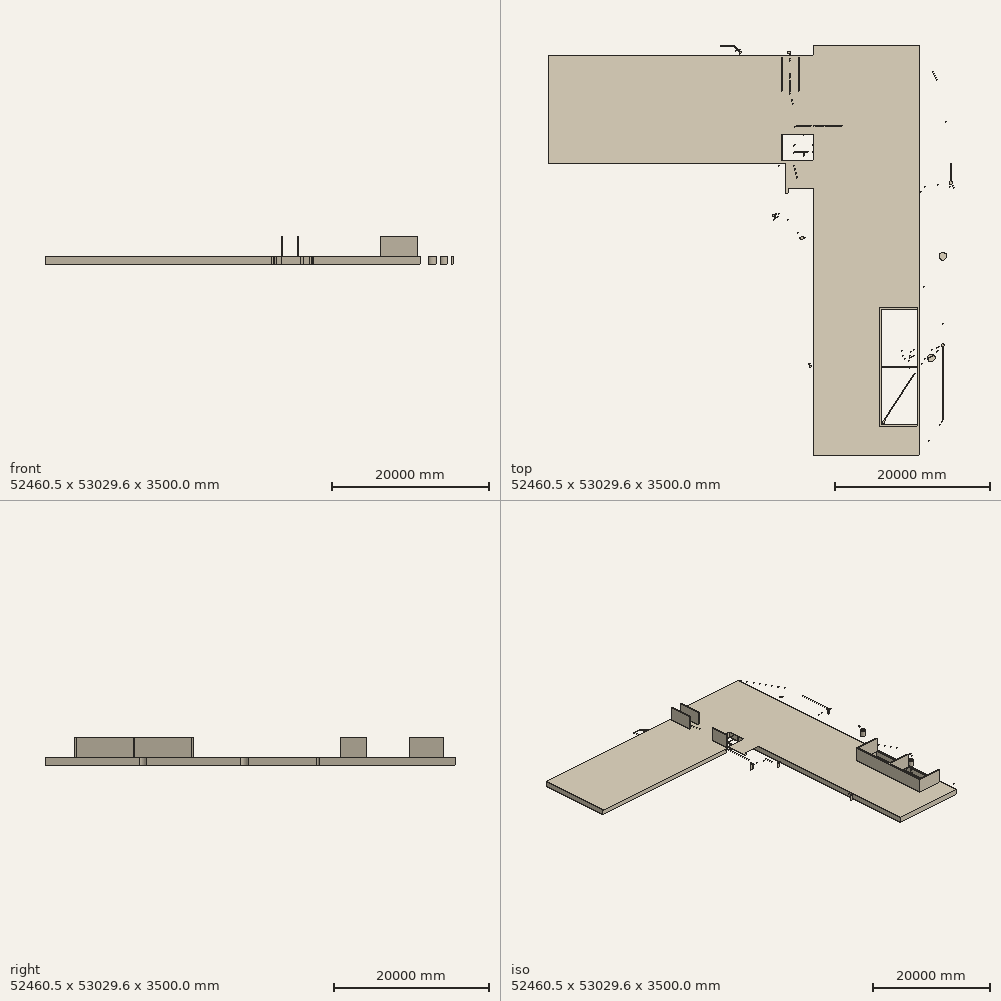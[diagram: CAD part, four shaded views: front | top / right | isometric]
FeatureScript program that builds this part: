
annotation { "Feature Type Name" : "Feature", "Feature Type Description" : "" }
export const myFeature = defineFeature(function(context is Context, id is Id, definition is map)
    precondition{}
    {
        {
            var Q0;
            Q0=qCreatedBy(makeId("Top.planeOp"),FACE);
            var sketch = newSketch(context, id + "F0", { "sketchPlane" : qUnion([Q0])});
            skLineSegment(sketch, "E0", {"start": v(56364.8, 6468.58) * mm, "end": v(56364.8, -31331.42) * mm});
            skLineSegment(sketch, "E1", {"start": v(56364.8, 6468.58) * mm, "end": v(22064.8, 6468.58) * mm});
            skLineSegment(sketch, "E2", {"start": v(56364.8, -31331.42) * mm, "end": v(70064.8, -31331.42) * mm});
            skLineSegment(sketch, "E3", {"start": v(70064.8, -31331.42) * mm, "end": v(70064.8, 21668.58) * mm});
            skLineSegment(sketch, "E4", {"start": v(70064.8, 21668.58) * mm, "end": v(56364.8, 21668.58) * mm});
            skLineSegment(sketch, "E5", {"start": v(22064.8, 20468.58) * mm, "end": v(22064.8, 6468.58) * mm});
            skPoint(sketch, "E6", {"position": v(56364.8, 21668.58) * mm});
            skLineSegment(sketch, "E7", {"start": v(56364.8, 21668.58) * mm, "end": v(56364.8, 20468.58) * mm});
            skLineSegment(sketch, "E8", {"start": v(56364.8, 20468.58) * mm, "end": v(22064.8, 20468.58) * mm});
            skPoint(sketch, "E9", {"position": v(56364.8, 20168.58) * mm});
            skPoint(sketch, "E10", {"position": v(56366.57, 6768.58) * mm});
            skLineSegment(sketch, "E11", {"start": v(56366.57, 6768.58) * mm, "end": v(22064.8, 6768.58) * mm});
            skLineSegment(sketch, "E12", {"start": v(56364.8, 20168.58) * mm, "end": v(22064.8, 20168.58) * mm});
            skLineSegment(sketch, "E13", {"start": v(52221.8, 20168.58) * mm, "end": v(52221.8, 15726.58) * mm});
            skPoint(sketch, "E14", {"position": v(52221.8, 20168.58) * mm});
            skLineSegment(sketch, "E15", {"start": v(52341.8, 20168.58) * mm, "end": v(52341.8, 15726.58) * mm});
            skLineSegment(sketch, "E16", {"start": v(54356.8, 20168.58) * mm, "end": v(54356.8, 15726.58) * mm});
            skLineSegment(sketch, "E17", {"start": v(54476.8, 20168.58) * mm, "end": v(54476.8, 15726.58) * mm});
            skLineSegment(sketch, "E18", {"start": v(56364.8, 6468.58) * mm, "end": v(56364.8, 10201.58) * mm});
            skLineSegment(sketch, "E19", {"start": v(56364.8, 10201.58) * mm, "end": v(52221.8, 10201.58) * mm});
            skLineSegment(sketch, "E20", {"start": v(52221.8, 10201.58) * mm, "end": v(52221.8, 6768.58) * mm});
            skLineSegment(sketch, "E21", {"start": v(52341.8, 10201.58) * mm, "end": v(52341.8, 6768.58) * mm});
            skLineSegment(sketch, "E22", {"start": v(69714.8, -12436.42) * mm, "end": v(65114.8, -12436.42) * mm});
            skLineSegment(sketch, "E23", {"start": v(69714.8, -27316.42) * mm, "end": v(65114.8, -27316.42) * mm});
            skLineSegment(sketch, "E24", {"start": v(69714.8, -31331.42) * mm, "end": v(69714.8, 21668.58) * mm});
            skPoint(sketch, "E25", {"position": v(70064.8, -19876.42) * mm});
            skLineSegment(sketch, "E26", {"start": v(69714.8, -19756.42) * mm, "end": v(65114.8, -19756.42) * mm});
            skLineSegment(sketch, "E27", {"start": v(69714.8, -19996.42) * mm, "end": v(65114.8, -19996.42) * mm});
            skPoint(sketch, "E28.orphan", {"position": v(47856.69, 10201.58) * mm});
            skPoint(sketch, "E29.orphan", {"position": v(52341.8, 11812.01) * mm});
            skLineSegment(sketch, "E30", {"start": v(52221.8, 15726.58) * mm, "end": v(52341.8, 15726.58) * mm});
            skLineSegment(sketch, "E31", {"start": v(54356.8, 15726.58) * mm, "end": v(54476.8, 15726.58) * mm});
            skLineSegment(sketch, "E32", {"start": v(65114.8, -19996.42) * mm, "end": v(65114.8, -19756.42) * mm});
            skLineSegment(sketch, "E33", {"start": v(65114.8, -12436.42) * mm, "end": v(65114.8, -12196.42) * mm});
            skLineSegment(sketch, "E34", {"start": v(65114.8, -12196.42) * mm, "end": v(69714.8, -12196.42) * mm});
            skLineSegment(sketch, "E35", {"start": v(65114.8, -27316.42) * mm, "end": v(65114.8, -27556.42) * mm});
            skLineSegment(sketch, "E36", {"start": v(65114.8, -27556.42) * mm, "end": v(69714.8, -27556.42) * mm});
            skLineSegment(sketch, "E37.bottom", {"start": v(65114.8, -12196.42) * mm, "end": v(64874.8, -12196.42) * mm});
            skLineSegment(sketch, "E37.top", {"start": v(65114.8, -27556.42) * mm, "end": v(64874.8, -27556.42) * mm});
            skLineSegment(sketch, "E37.left", {"start": v(65114.8, -12196.42) * mm, "end": v(65114.8, -27556.42) * mm});
            skLineSegment(sketch, "E37.right", {"start": v(64874.8, -12196.42) * mm, "end": v(64874.8, -27556.42) * mm});
            skLineSegment(sketch, "E38", {"start": v(52664.8, 3178.58) * mm, "end": v(56364.8, 3178.58) * mm});
            skLineSegment(sketch, "E39.trimOffspring", {"start": v(52664.8, 6468.58) * mm, "end": v(52664.8, 3178.58) * mm});
            skLineSegment(sketch, "E40.bottom", {"start": v(52664.8, 3178.58) * mm, "end": v(53121.8, 3178.58) * mm});
            skLineSegment(sketch, "E40.top", {"start": v(52664.8, 2595.58) * mm, "end": v(53121.8, 2595.58) * mm});
            skLineSegment(sketch, "E40.left", {"start": v(52664.8, 3178.58) * mm, "end": v(52664.8, 2595.58) * mm});
            skLineSegment(sketch, "E40.right", {"start": v(53121.8, 3178.58) * mm, "end": v(53121.8, 2595.58) * mm});
            skSolve(sketch);
        }
        {
            var Q0;
            Q0=qCreatedBy(makeId("Top.planeOp"),FACE);
            var sketch = newSketch(context, id + "F1", { "sketchPlane" : qUnion([Q0])});
            skLineSegment(sketch, "E41", {"start": v(53664.8, 6468.58) * mm, "end": v(54182.45, 4536.73) * mm});
            skPoint(sketch, "E42", {"position": v(53664.8, 6468.58) * mm});
            skLineSegment(sketch, "E43", {"start": v(54182.45, 4536.73) * mm, "end": v(54182.45, -2463.27) * mm});
            skLineSegment(sketch, "E44", {"start": v(53828.9, -1109.71) * mm, "end": v(54182.45, -1463.27) * mm});
            skPoint(sketch, "E45", {"position": v(54182.45, -1463.27) * mm});
            skCircle(sketch, "E46", {"center": v(54864.8, -3240.9) * mm, "radius": 212.5 * mm});
            skPoint(sketch, "E47", {"position": v(54857.37, -3028.53) * mm});
            skLineSegment(sketch, "E48", {"start": v(54182.45, -2463.27) * mm, "end": v(54864.44, -3034.46) * mm});
            skPoint(sketch, "E49", {"position": v(70139.8, -8631.42) * mm});
            skPoint(sketch, "E50", {"position": v(73064.8, -26831.42) * mm});
            skLineSegment(sketch, "E51", {"start": v(70139.8, -31081.42) * mm, "end": v(73064.8, -26831.42) * mm});
            skPoint(sketch, "E52", {"position": v(73064.8, -17081.42) * mm});
            skPoint(sketch, "E53", {"position": v(73064.8, -14331.42) * mm});
            skCircle(sketch, "E54", {"center": v(73064.8, -17081.42) * mm, "radius": 212.5 * mm});
            skLineSegment(sketch, "E55", {"start": v(73064.8, -26831.42) * mm, "end": v(73064.8, -17293.92) * mm});
            skLineSegment(sketch, "E56", {"start": v(70139.8, -8631.42) * mm, "end": v(73064.8, -14331.42) * mm});
            skLineSegment(sketch, "E57", {"start": v(73064.8, -14331.42) * mm, "end": v(73064.8, -16868.92) * mm});
            skPoint(sketch, "E58", {"position": v(71564.8, -18731.42) * mm});
            skCircle(sketch, "E59", {"center": v(71564.8, -18731.42) * mm, "radius": 500 * mm});
            skLineSegment(sketch, "E60", {"start": v(72921.87, -17238.65) * mm, "end": v(71901.15, -18361.45) * mm});
            skPoint(sketch, "E61", {"position": v(73064.8, -5581.42) * mm});
            skPoint(sketch, "E62", {"position": v(74064.8, -2831.42) * mm});
            skPoint(sketch, "E63", {"position": v(74064.8, 11668.58) * mm});
            skPoint(sketch, "E64", {"position": v(74064.8, 3918.58) * mm});
            skPoint(sketch, "E65", {"position": v(74064.8, 13768.58) * mm});
            skCircle(sketch, "E66", {"center": v(74064.8, 3918.58) * mm, "radius": 212.5 * mm});
            skLineSegment(sketch, "E67", {"start": v(70139.8, 2668.58) * mm, "end": v(70729.42, 3400.6) * mm});
            skLineSegment(sketch, "E68", {"start": v(70729.42, 3400.6) * mm, "end": v(73854.83, 3885.97) * mm});
            skCircle(sketch, "E69", {"center": v(73064.8, -5581.42) * mm, "radius": 500 * mm});
            skLineSegment(sketch, "E70", {"start": v(73064.8, -5581.42) * mm, "end": v(74064.8, -2831.42) * mm});
            skLineSegment(sketch, "E71", {"start": v(74064.8, 3918.58) * mm, "end": v(74064.8, -2831.42) * mm});
            skLineSegment(sketch, "E72", {"start": v(74064.8, 3918.58) * mm, "end": v(74064.8, 11668.58) * mm});
            skLineSegment(sketch, "E73", {"start": v(74064.8, 11668.58) * mm, "end": v(74064.8, 13768.58) * mm});
            skLineSegment(sketch, "E74", {"start": v(74064.8, 13768.58) * mm, "end": v(70139.8, 21418.58) * mm});
            skLineSegment(sketch, "E75", {"start": v(70139.8, 13768.58) * mm, "end": v(71421.55, 12224.42) * mm});
            skLineSegment(sketch, "E76", {"start": v(71421.55, 12224.42) * mm, "end": v(74064.8, 11668.58) * mm});
            skPoint(sketch, "E77", {"position": v(51114.8, -281.42) * mm});
            skLineSegment(sketch, "E78", {"start": v(51114.8, -281.42) * mm, "end": v(53828.9, -1109.71) * mm});
            skCircle(sketch, "E79", {"center": v(51114.8, -281.42) * mm, "radius": 157.5 * mm});
            skLineSegment(sketch, "E80", {"start": v(51567.38, 60.2) * mm, "end": v(51296.06, -828.82) * mm});
            skLineSegment(sketch, "E81", {"start": v(51296.06, -828.82) * mm, "end": v(51894.17, -35.98) * mm});
            skPoint(sketch, "E82", {"position": v(51597.82, -428.82) * mm});
            skPoint(sketch, "E83", {"position": v(51433.45, -378.66) * mm});
            skPoint(sketch, "E84", {"position": v(51265.45, -327.39) * mm});
            skPoint(sketch, "E85", {"position": v(56214.8, -19831.42) * mm});
            skPoint(sketch, "E86", {"position": v(55964.8, -19831.42) * mm});
            skCircle(sketch, "E87", {"center": v(55964.8, -19831.42) * mm, "radius": 157.5 * mm});
            skLineSegment(sketch, "E88", {"start": v(55439.22, -19965.06) * mm, "end": v(56064.44, -19277.27) * mm});
            skLineSegment(sketch, "E89", {"start": v(56064.44, -19277.27) * mm, "end": v(55184.87, -19738.45) * mm});
            skPoint(sketch, "E90", {"position": v(55635.54, -19502.15) * mm});
            skLineSegment(sketch, "E91", {"start": v(55964.8, -19831.42) * mm, "end": v(55214.8, -19081.42) * mm});
            skPoint(sketch, "E92", {"position": v(55853.44, -19720.05) * mm});
            skPoint(sketch, "E93", {"position": v(55807.3, -19831.42) * mm});
            skLineSegment(sketch, "E94", {"start": v(70139.8, -19831.42) * mm, "end": v(71387.08, -17771.2) * mm});
            skLineSegment(sketch, "E95", {"start": v(71387.08, -17771.2) * mm, "end": v(72868.27, -17162.22) * mm});
            skPoint(sketch, "E96", {"position": v(72868.27, -17162.22) * mm});
            skPoint(sketch, "E97", {"position": v(55753.13, -19619.74) * mm});
            skLineSegment(sketch, "E98", {"start": v(47864.8, 6318.58) * mm, "end": v(51563.3, 6318.58) * mm});
            skLineSegment(sketch, "E99", {"start": v(51563.3, 6318.58) * mm, "end": v(51917.8, 6030.87) * mm});
            skLineSegment(sketch, "E100", {"start": v(51917.8, 6030.87) * mm, "end": v(51917.8, 619.15) * mm});
            skLineSegment(sketch, "E101", {"start": v(51917.8, 619.15) * mm, "end": v(51114.8, -281.42) * mm});
            skPoint(sketch, "E102", {"position": v(51917.8, 2559.53) * mm});
            skLineSegment(sketch, "E103", {"start": v(51917.8, 2559.53) * mm, "end": v(52279.66, 2921.39) * mm});
            skLineSegment(sketch, "E104", {"start": v(52279.66, 2921.39) * mm, "end": v(52811.8, 2921.39) * mm});
            skPoint(sketch, "E105", {"position": v(46851.2, 20733.64) * mm});
            skCircle(sketch, "E106", {"center": v(46851.2, 20733.64) * mm, "radius": 157.5 * mm});
            skLineSegment(sketch, "E107", {"start": v(46325.62, 20600) * mm, "end": v(46950.83, 21287.79) * mm});
            skLineSegment(sketch, "E108", {"start": v(46950.83, 21287.79) * mm, "end": v(46071.27, 20826.6) * mm});
            skPoint(sketch, "E109", {"position": v(46521.94, 21062.9) * mm});
            skLineSegment(sketch, "E110", {"start": v(46851.2, 20733.64) * mm, "end": v(45951.46, 21633.38) * mm});
            skPoint(sketch, "E111", {"position": v(46739.84, 20845) * mm});
            skPoint(sketch, "E112", {"position": v(46693.7, 20733.64) * mm});
            skCircle(sketch, "E113", {"center": v(46664.8, 20543.58) * mm, "radius": 55 * mm});
            skPoint(sketch, "E114", {"position": v(46639.53, 20945.32) * mm});
            skLineSegment(sketch, "E115", {"start": v(44664.8, 19768.58) * mm, "end": v(44664.8, 21465.21) * mm});
            skLineSegment(sketch, "E116", {"start": v(45951.46, 21633.38) * mm, "end": v(44322.18, 21633.38) * mm});
            skLineSegment(sketch, "E117", {"start": v(44664.8, 21465.21) * mm, "end": v(44496.64, 21633.38) * mm});
            skCircle(sketch, "E118", {"center": v(44727.7, 20131.27) * mm, "radius": 25 * mm, "construction": true});
            skLineSegment(sketch, "E119", {"start": v(44727.7, 20131.27) * mm, "end": v(44664.8, 19768.58) * mm});
            skCircle(sketch, "E120", {"center": v(53556.8, 20018.58) * mm, "radius": 55 * mm});
            skCircle(sketch, "E121", {"center": v(54282.28, 18938.58) * mm, "radius": 55 * mm});
            skCircle(sketch, "E122", {"center": v(54282.28, 16918.58) * mm, "radius": 55 * mm});
            skPoint(sketch, "E123", {"position": v(52741.8, 19768.58) * mm});
            skLineSegment(sketch, "E124.bottom", {"start": v(52681.3, 19855.08) * mm, "end": v(52802.3, 19855.08) * mm});
            skLineSegment(sketch, "E124.top", {"start": v(52681.3, 19682.08) * mm, "end": v(52802.3, 19682.08) * mm});
            skLineSegment(sketch, "E124.left", {"start": v(52681.3, 19855.08) * mm, "end": v(52681.3, 19682.08) * mm});
            skLineSegment(sketch, "E124.right", {"start": v(52802.3, 19855.08) * mm, "end": v(52802.3, 19682.08) * mm});
            skLineSegment(sketch, "E125", {"start": v(53195.46, 20793.39) * mm, "end": v(53195.46, 15712.6) * mm});
            skLineSegment(sketch, "E126", {"start": v(53195.46, 15712.6) * mm, "end": v(53664.8, 14001.77) * mm});
            skLineSegment(sketch, "E127", {"start": v(53664.8, 14001.77) * mm, "end": v(53664.8, 6468.58) * mm});
            skLineSegment(sketch, "E128", {"start": v(54282.28, 16918.58) * mm, "end": v(53445.11, 16918.58) * mm});
            skLineSegment(sketch, "E129", {"start": v(53445.11, 16918.58) * mm, "end": v(53195.46, 16668.93) * mm});
            skLineSegment(sketch, "E130", {"start": v(54282.28, 18938.58) * mm, "end": v(53415.44, 18938.58) * mm});
            skLineSegment(sketch, "E131", {"start": v(53415.44, 18938.58) * mm, "end": v(53195.46, 18718.6) * mm});
            skLineSegment(sketch, "E132", {"start": v(53556.8, 20018.58) * mm, "end": v(53302.98, 20018.58) * mm});
            skLineSegment(sketch, "E133", {"start": v(53302.98, 20018.58) * mm, "end": v(53195.46, 19911.06) * mm});
            skCircle(sketch, "E134", {"center": v(53671.8, 6828.9) * mm, "radius": 55 * mm});
            skCircle(sketch, "E135", {"center": v(55041.8, 6828.9) * mm, "radius": 55 * mm});
            skCircle(sketch, "E136", {"center": v(56214.8, 8864.58) * mm, "radius": 55 * mm});
            skCircle(sketch, "E137", {"center": v(56214.8, 7944.58) * mm, "radius": 55 * mm});
            skCircle(sketch, "E138", {"center": v(52396.8, 9538.58) * mm, "radius": 55 * mm});
            skCircle(sketch, "E139", {"center": v(55041.8, 10146.58) * mm, "radius": 55 * mm});
            skLineSegment(sketch, "E140", {"start": v(56214.8, 7944.58) * mm, "end": v(53914.8, 7944.58) * mm});
            skLineSegment(sketch, "E141", {"start": v(53914.8, 7944.58) * mm, "end": v(53914.8, 7944.58) * mm});
            skLineSegment(sketch, "E142", {"start": v(53914.8, 7944.58) * mm, "end": v(53664.8, 7694.58) * mm});
            skLineSegment(sketch, "E143", {"start": v(56214.8, 8864.58) * mm, "end": v(53914.8, 8864.58) * mm});
            skLineSegment(sketch, "E144", {"start": v(53914.8, 8864.58) * mm, "end": v(53664.8, 8614.58) * mm});
            skLineSegment(sketch, "E145", {"start": v(55041.8, 10146.58) * mm, "end": v(55041.8, 8979.55) * mm});
            skLineSegment(sketch, "E146", {"start": v(55041.8, 8979.55) * mm, "end": v(54926.84, 8864.58) * mm});
            skLineSegment(sketch, "E147", {"start": v(55041.8, 6828.9) * mm, "end": v(55041.8, 7817.77) * mm});
            skLineSegment(sketch, "E148", {"start": v(55041.8, 7817.77) * mm, "end": v(54915, 7944.58) * mm});
            skLineSegment(sketch, "E149", {"start": v(52396.8, 9538.58) * mm, "end": v(53591.64, 9538.58) * mm});
            skLineSegment(sketch, "E150", {"start": v(53591.64, 9538.58) * mm, "end": v(53664.8, 9465.4) * mm});
            skCircle(sketch, "E151", {"center": v(60014.8, 11278.58) * mm, "radius": 55 * mm});
            skLineSegment(sketch, "E152", {"start": v(60014.8, 11278.58) * mm, "end": v(54006.65, 11278.58) * mm});
            skLineSegment(sketch, "E153", {"start": v(54006.65, 11278.58) * mm, "end": v(53664.8, 10936.75) * mm});
            skCircle(sketch, "E154", {"center": v(53195.46, 20793.39) * mm, "radius": 200 * mm});
            skCircle(sketch, "E155", {"center": v(67706.8, -18221.42) * mm, "radius": 55 * mm});
            skCircle(sketch, "E156", {"center": v(67706.8, -17821.42) * mm, "radius": 55 * mm});
            skCircle(sketch, "E157", {"center": v(68354.8, -18121.42) * mm, "radius": 25 * mm});
            skCircle(sketch, "E158", {"center": v(68354.8, -17921.42) * mm, "radius": 25 * mm});
            skCircle(sketch, "E159", {"center": v(69314.8, -18471.42) * mm, "radius": 55 * mm});
            skCircle(sketch, "E160", {"center": v(69314.8, -17671.42) * mm, "radius": 55 * mm});
            skLineSegment(sketch, "E161", {"start": v(69214.8, -20746.42) * mm, "end": v(69714.8, -20746.42) * mm});
            skLineSegment(sketch, "E162", {"start": v(69214.8, -20746.42) * mm, "end": v(68030.87, -18628.96) * mm});
            skLineSegment(sketch, "E163", {"start": v(68030.87, -18628.96) * mm, "end": v(68030.87, -12507) * mm});
            skLineSegment(sketch, "E164", {"start": v(67706.8, -18221.42) * mm, "end": v(68030.87, -18628.96) * mm});
            skLineSegment(sketch, "E165", {"start": v(68354.8, -18121.42) * mm, "end": v(68445.6, -18254.83) * mm});
            skLineSegment(sketch, "E166", {"start": v(68445.6, -18254.83) * mm, "end": v(68445.6, -19370.69) * mm});
            skLineSegment(sketch, "E167", {"start": v(68445.6, -18254.83) * mm, "end": v(68445.6, -18012.45) * mm});
            skLineSegment(sketch, "E168", {"start": v(68354.8, -17921.42) * mm, "end": v(68445.6, -18012.45) * mm});
            skLineSegment(sketch, "E169", {"start": v(68554.52, -19565.5) * mm, "end": v(68889.6, -17921.42) * mm});
            skLineSegment(sketch, "E170", {"start": v(68889.6, -17921.42) * mm, "end": v(69314.8, -17671.42) * mm});
            skLineSegment(sketch, "E171", {"start": v(69314.8, -18471.42) * mm, "end": v(68719.14, -18757.76) * mm});
            skLineSegment(sketch, "E172", {"start": v(67706.8, -17821.42) * mm, "end": v(68030.87, -18145.47) * mm});
            skLineSegment(sketch, "E173", {"start": v(51894.17, -35.98) * mm, "end": v(51910.14, -48.03) * mm});
            skLineSegment(sketch, "E174", {"start": v(51910.14, -48.03) * mm, "end": v(51139.5, -1069.56) * mm});
            skLineSegment(sketch, "E175", {"start": v(51139.5, -1069.56) * mm, "end": v(51375.94, -92.84) * mm});
            skLineSegment(sketch, "E176", {"start": v(51375.94, -92.84) * mm, "end": v(51567.38, 60.2) * mm});
            skLineSegment(sketch, "E177", {"start": v(51265.45, -327.39) * mm, "end": v(51256.86, -345.45) * mm});
            skLineSegment(sketch, "E178", {"start": v(51256.86, -345.45) * mm, "end": v(53828.9, -1130.4) * mm});
            skLineSegment(sketch, "E179", {"start": v(53828.9, -1130.4) * mm, "end": v(54255.94, -1463.27) * mm});
            skLineSegment(sketch, "E180", {"start": v(54255.94, -1463.27) * mm, "end": v(54255.94, -2466.34) * mm});
            skLineSegment(sketch, "E181", {"start": v(54255.94, -2466.34) * mm, "end": v(54837.71, -3030.14) * mm});
            skLineSegment(sketch, "E182", {"start": v(54837.71, -3030.14) * mm, "end": v(54842.1, -3015.75) * mm});
            skLineSegment(sketch, "E183", {"start": v(54230.53, 4574.46) * mm, "end": v(53723, 6468.58) * mm});
            skLineSegment(sketch, "E184", {"start": v(53723, 6468.58) * mm, "end": v(53723, 9407.22) * mm});
            skLineSegment(sketch, "E185", {"start": v(53723, 9407.22) * mm, "end": v(53591.64, 9523.95) * mm});
            skLineSegment(sketch, "E186", {"start": v(53591.64, 9523.95) * mm, "end": v(52451.34, 9531.43) * mm});
            skLineSegment(sketch, "E187", {"start": v(53723, 9407.22) * mm, "end": v(53723, 14001.77) * mm});
            skLineSegment(sketch, "E188", {"start": v(53723, 14001.77) * mm, "end": v(53285.39, 15596.9) * mm});
            skLineSegment(sketch, "E189", {"start": v(53285.39, 15596.9) * mm, "end": v(53285.39, 20793.39) * mm});
            skLineSegment(sketch, "E190", {"start": v(53195.46, 20793.39) * mm, "end": v(53285.39, 20793.39) * mm});
            skLineSegment(sketch, "E191", {"start": v(53195.46, 19779.43) * mm, "end": v(53302.98, 20022.61) * mm});
            skLineSegment(sketch, "E192", {"start": v(53302.98, 20022.61) * mm, "end": v(53508.1, 20022.61) * mm});
            skLineSegment(sketch, "E193", {"start": v(53285.39, 19246.98) * mm, "end": v(52741.8, 19682.08) * mm});
            skLineSegment(sketch, "E194", {"start": v(52808.1, 19682.08) * mm, "end": v(52741.8, 19682.08) * mm});
            skLineSegment(sketch, "E195", {"start": v(52808.1, 19682.08) * mm, "end": v(53285.39, 19300.04) * mm});
            skLineSegment(sketch, "E196", {"start": v(53195.46, 18593.88) * mm, "end": v(53415.44, 18813.86) * mm});
            skLineSegment(sketch, "E197", {"start": v(53415.44, 18813.86) * mm, "end": v(54227.82, 18946.25) * mm});
            skLineSegment(sketch, "E198", {"start": v(54227.82, 18946.25) * mm, "end": v(54227.82, 18938.58) * mm});
            skLineSegment(sketch, "E199", {"start": v(53195.46, 16678.13) * mm, "end": v(53445.11, 16927.8) * mm});
            skLineSegment(sketch, "E200", {"start": v(53445.11, 16927.8) * mm, "end": v(54228.06, 16927.8) * mm});
            skLineSegment(sketch, "E201", {"start": v(54228.06, 16927.8) * mm, "end": v(54228.06, 16918.58) * mm});
            skLineSegment(sketch, "E202", {"start": v(53664.8, 10815.59) * mm, "end": v(54141.36, 11292.14) * mm});
            skLineSegment(sketch, "E203", {"start": v(54141.36, 11292.14) * mm, "end": v(59961.5, 11292.14) * mm});
            skLineSegment(sketch, "E204", {"start": v(53664.8, 8487.7) * mm, "end": v(54058.01, 8880.9) * mm});
            skLineSegment(sketch, "E205", {"start": v(54058.01, 8880.9) * mm, "end": v(56162.29, 8880.9) * mm});
            skLineSegment(sketch, "E206", {"start": v(54957.2, 8880.9) * mm, "end": v(55055.85, 8979.55) * mm});
            skLineSegment(sketch, "E207", {"start": v(55055.85, 8979.55) * mm, "end": v(55055.85, 10093.4) * mm});
            skLineSegment(sketch, "E208", {"start": v(53664.8, 7573.72) * mm, "end": v(53914.8, 7823.72) * mm});
            skLineSegment(sketch, "E209", {"start": v(53914.8, 7823.72) * mm, "end": v(56160.57, 7953.72) * mm});
            skLineSegment(sketch, "E210", {"start": v(55007.74, 7944.58) * mm, "end": v(55130.8, 7821.52) * mm});
            skLineSegment(sketch, "E211", {"start": v(55130.8, 7821.52) * mm, "end": v(55048.1, 6883.54) * mm});
            skCircle(sketch, "E212", {"center": v(52811.8, 2921.39) * mm, "radius": 55 * mm});
            skCircle(sketch, "E213", {"center": v(47864.8, 6318.58) * mm, "radius": 55 * mm});
            skLineSegment(sketch, "E214", {"start": v(47916.55, 6337.23) * mm, "end": v(51599.4, 6337.23) * mm});
            skLineSegment(sketch, "E215", {"start": v(51599.4, 6337.23) * mm, "end": v(51960.4, 6044.25) * mm});
            skLineSegment(sketch, "E216", {"start": v(51960.4, 6044.25) * mm, "end": v(51960.4, 618.5) * mm});
            skLineSegment(sketch, "E217", {"start": v(51960.4, 618.5) * mm, "end": v(51241.46, -187.78) * mm});
            skLineSegment(sketch, "E218", {"start": v(51960.4, 2652.07) * mm, "end": v(52260.98, 2952.66) * mm});
            skLineSegment(sketch, "E219", {"start": v(52260.98, 2952.66) * mm, "end": v(52766.57, 2952.66) * mm});
            skCircle(sketch, "E220", {"center": v(70139.8, 21418.58) * mm, "radius": 55 * mm});
            skLineSegment(sketch, "E221", {"start": v(70177, 21378.07) * mm, "end": v(74081.22, 13768.58) * mm});
            skLineSegment(sketch, "E222", {"start": v(74081.22, 13768.58) * mm, "end": v(74103.95, 4127.45) * mm});
            skCircle(sketch, "E223", {"center": v(70139.8, 13768.58) * mm, "radius": 55 * mm});
            skLineSegment(sketch, "E224", {"start": v(70183.67, 13735.4) * mm, "end": v(71430.83, 12232.9) * mm});
            skLineSegment(sketch, "E225", {"start": v(71430.83, 12232.9) * mm, "end": v(74064.8, 11679.01) * mm});
            skCircle(sketch, "E226", {"center": v(70139.8, 2668.58) * mm, "radius": 55 * mm});
            skLineSegment(sketch, "E227", {"start": v(70185.41, 2699.33) * mm, "end": v(70744.22, 3393.1) * mm});
            skLineSegment(sketch, "E228", {"start": v(70744.22, 3393.1) * mm, "end": v(73857.72, 3870.95) * mm});
            skLineSegment(sketch, "E229", {"start": v(74468.89, 3565.15) * mm, "end": v(73838.01, 3370.7) * mm});
            skLineSegment(sketch, "E230", {"start": v(73838.01, 3370.7) * mm, "end": v(74521.95, 3252.85) * mm});
            skLineSegment(sketch, "E231", {"start": v(74521.95, 3252.85) * mm, "end": v(74525.35, 3272.58) * mm});
            skLineSegment(sketch, "E232", {"start": v(74525.35, 3272.58) * mm, "end": v(73931.39, 3374.93) * mm});
            skLineSegment(sketch, "E233", {"start": v(73931.39, 3374.93) * mm, "end": v(74484.63, 3545.45) * mm});
            skLineSegment(sketch, "E234", {"start": v(74484.63, 3545.45) * mm, "end": v(74468.89, 3565.15) * mm});
            skLineSegment(sketch, "E235", {"start": v(74064.8, 3706.08) * mm, "end": v(74061.14, -2826.14) * mm});
            skLineSegment(sketch, "E236", {"start": v(74061.14, -2826.14) * mm, "end": v(73230.74, -5109.75) * mm});
            skCircle(sketch, "E237", {"center": v(70139.8, -8631.42) * mm, "radius": 50 * mm});
            skLineSegment(sketch, "E238", {"start": v(70165.57, -8674.27) * mm, "end": v(73068.58, -14331.42) * mm});
            skLineSegment(sketch, "E239", {"start": v(73068.58, -14331.42) * mm, "end": v(73068.58, -16868.95) * mm});
            skLineSegment(sketch, "E240", {"start": v(73054.83, -17293.68) * mm, "end": v(73054.83, -26821.85) * mm});
            skLineSegment(sketch, "E241", {"start": v(73054.83, -26821.85) * mm, "end": v(70165.62, -31032.85) * mm});
            skCircle(sketch, "E242", {"center": v(70139.8, -31081.42) * mm, "radius": 55 * mm});
            skLineSegment(sketch, "E243", {"start": v(72939.48, -17253.02) * mm, "end": v(71917.6, -18377.1) * mm});
            skLineSegment(sketch, "E244", {"start": v(72662.5, -17518.06) * mm, "end": v(73067.36, -17675.19) * mm});
            skLineSegment(sketch, "E245", {"start": v(73067.36, -17675.19) * mm, "end": v(73060.52, -17692.82) * mm});
            skLineSegment(sketch, "E246", {"start": v(73060.52, -17692.82) * mm, "end": v(72688.36, -17548.38) * mm});
            skLineSegment(sketch, "E247", {"start": v(72688.36, -17548.38) * mm, "end": v(72884.6, -18001.24) * mm});
            skLineSegment(sketch, "E248", {"start": v(72884.6, -18001.24) * mm, "end": v(72866.1, -18021.59) * mm});
            skLineSegment(sketch, "E249", {"start": v(72866.1, -18021.59) * mm, "end": v(72662.5, -17518.06) * mm});
            skLineSegment(sketch, "E250", {"start": v(72881.28, -17188.53) * mm, "end": v(71387.08, -17802.86) * mm});
            skLineSegment(sketch, "E251", {"start": v(71387.08, -17802.86) * mm, "end": v(70181.02, -19795) * mm});
            skCircle(sketch, "E252", {"center": v(70139.8, -19831.42) * mm, "radius": 55 * mm});
            skLineSegment(sketch, "E253", {"start": v(69714.8, -20746.42) * mm, "end": v(69714.8, -20763.78) * mm});
            skLineSegment(sketch, "E254", {"start": v(69714.8, -20763.78) * mm, "end": v(69209.7, -20763.78) * mm});
            skLineSegment(sketch, "E255", {"start": v(69209.7, -20763.78) * mm, "end": v(68126.06, -18825.7) * mm});
            skLineSegment(sketch, "E256", {"start": v(68126.06, -18825.7) * mm, "end": v(67731.48, -18270.57) * mm});
            skLineSegment(sketch, "E257", {"start": v(68140.87, -18825.7) * mm, "end": v(68140.87, -12507) * mm});
            skLineSegment(sketch, "E258", {"start": v(68140.87, -12507) * mm, "end": v(68030.87, -12507) * mm});
            skLineSegment(sketch, "E259", {"start": v(68030.87, -18134.71) * mm, "end": v(67750.7, -17854.55) * mm});
            skLineSegment(sketch, "E260", {"start": v(68490.86, -19451.64) * mm, "end": v(68460.44, -18005.31) * mm});
            skLineSegment(sketch, "E261", {"start": v(68460.44, -18005.31) * mm, "end": v(68379.64, -17924.3) * mm});
            skLineSegment(sketch, "E262", {"start": v(68445.6, -18258.5) * mm, "end": v(68367.12, -18143.17) * mm});
            skLineSegment(sketch, "E263", {"start": v(68584.13, -19618.45) * mm, "end": v(68922.9, -17956.2) * mm});
            skLineSegment(sketch, "E264", {"start": v(68922.9, -17956.2) * mm, "end": v(69313.76, -17726.4) * mm});
            skLineSegment(sketch, "E265", {"start": v(68722.06, -18743.46) * mm, "end": v(69261.32, -18484.23) * mm});
            skLineSegment(sketch, "E266", {"start": v(55853.44, -19720.05) * mm, "end": v(55214.8, -19093.76) * mm});
            skLineSegment(sketch, "E267", {"start": v(55214.8, -19093.76) * mm, "end": v(55214.8, -19081.42) * mm});
            skLineSegment(sketch, "E268", {"start": v(55184.87, -19738.45) * mm, "end": v(55177.02, -19730.6) * mm});
            skLineSegment(sketch, "E269", {"start": v(55177.02, -19730.6) * mm, "end": v(56081.23, -19256.5) * mm});
            skLineSegment(sketch, "E270", {"start": v(56081.23, -19256.5) * mm, "end": v(55439.22, -19983.88) * mm});
            skLineSegment(sketch, "E271", {"start": v(55439.22, -19983.88) * mm, "end": v(55439.45, -19965.22) * mm});
            skCircle(sketch, "E272", {"center": v(56214.8, -19831.42) * mm, "radius": 55 * mm});
            skCircle(sketch, "E273", {"center": v(65189.8, -27241.42) * mm, "radius": 55 * mm});
            skCircle(sketch, "E274", {"center": v(65417.45, -27241.42) * mm, "radius": 55 * mm});
            skLineSegment(sketch, "E275.left", {"start": v(65143.85, -27211.2) * mm, "end": v(69330.85, -20763.78) * mm});
            skLineSegment(sketch, "E275.right", {"start": v(65236.1, -27271.12) * mm, "end": v(65434.35, -26965.84) * mm});
            skLineSegment(sketch, "E276.trimOffspring", {"start": v(65434.35, -26965.84) * mm, "end": v(65364.32, -27227.18) * mm});
            skLineSegment(sketch, "E277.trimOffspring", {"start": v(65628.22, -26667.3) * mm, "end": v(69462.01, -20763.78) * mm});
            skLineSegment(sketch, "E278.trimOffspring", {"start": v(65628.22, -26667.3) * mm, "end": v(65470.58, -27255.65) * mm});
            skLineSegment(sketch, "E279", {"start": v(65143.85, -27211.2) * mm, "end": v(65236.1, -27271.12) * mm});
            skPoint(sketch, "E280", {"position": v(68085.87, -12507) * mm});
            skCircle(sketch, "E281", {"center": v(68085.87, -12507) * mm, "radius": 55 * mm});
            skLineSegment(sketch, "E282.bottom", {"start": v(54464.8, -3160.9) * mm, "end": v(55264.8, -3160.9) * mm});
            skLineSegment(sketch, "E282.top", {"start": v(54464.8, -3320.9) * mm, "end": v(55264.8, -3320.9) * mm});
            skLineSegment(sketch, "E282.left", {"start": v(54464.8, -3160.9) * mm, "end": v(54464.8, -3320.9) * mm});
            skLineSegment(sketch, "E282.right", {"start": v(55264.8, -3160.9) * mm, "end": v(55264.8, -3320.9) * mm});
            skPoint(sketch, "E283", {"position": v(54864.8, -3160.9) * mm});
            skLineSegment(sketch, "E284", {"start": v(54230.53, 4574.46) * mm, "end": v(54255.94, -1463.27) * mm});
            skCircle(sketch, "E285", {"center": v(44664.8, 19768.58) * mm, "radius": 55 * mm});
            skLineSegment(sketch, "E286", {"start": v(44719.6, 19773.45) * mm, "end": v(44719.6, 21482.11) * mm});
            skLineSegment(sketch, "E287", {"start": v(44719.6, 21482.11) * mm, "end": v(44575.76, 21633.38) * mm});
            skLineSegment(sketch, "E288", {"start": v(44322.18, 21633.38) * mm, "end": v(44322.18, 21698.18) * mm});
            skLineSegment(sketch, "E289", {"start": v(44322.18, 21698.18) * mm, "end": v(45981.93, 21698.18) * mm});
            skLineSegment(sketch, "E290", {"start": v(45981.93, 21698.18) * mm, "end": v(46794, 20880.38) * mm});
            skLineSegment(sketch, "E291", {"start": v(46071.27, 20826.6) * mm, "end": v(46040.42, 20885.44) * mm});
            skLineSegment(sketch, "E292", {"start": v(46040.42, 20885.44) * mm, "end": v(46985.9, 21326.07) * mm});
            skLineSegment(sketch, "E293", {"start": v(46985.9, 21326.07) * mm, "end": v(46421.61, 20600) * mm});
            skLineSegment(sketch, "E294", {"start": v(46421.61, 20600) * mm, "end": v(46325.62, 20600) * mm});
            skSolve(sketch);
        }
        {
            var Q0;
            {var subQ12=sQuery(id+"F0.wireOp",EDGE,"E0");Q0=makeQuery(id+"F0.imprint","IMPRINT",FACE,{"disambiguationData":[TD([[makeQuery(id+"F0.imprint","IMPRINT",EDGE,{"derivedFrom":subQ12}),1.0]])]});}
            var Q1;
            {var subQ0=sQuery(id+"F0.wireOp",EDGE,"E12");var subQ1=makeQuery(id+"F0.imprint","IMPRINT",VERTEX,{"disambiguationData":[OD(0.0)],"derivedFrom":subQ0});Q1=makeQuery(id+"F0.imprint","IMPRINT",FACE,{"disambiguationData":[TD([[makeQuery(id+"F0.imprint","IMPRINT",EDGE,{"disambiguationData":[TD([[subQ1,1.0]])],"derivedFrom":subQ0}),-1.0]])]});}
            var Q2;
            {var subQ5=sQuery(id+"F0.wireOp",EDGE,"E3");Q2=makeQuery(id+"F0.imprint","IMPRINT",FACE,{"disambiguationData":[TD([[makeQuery(id+"F0.imprint","IMPRINT",EDGE,{"derivedFrom":subQ5}),1.0]])]});}
            var Q3;
            Q3=makeQuery(id+"F1.imprint","IMPRINT",FACE,{"disambiguationData":[TD([[makeQuery(id+"F1.imprint","IMPRINT",EDGE,{"derivedFrom":sQuery(id+"F1.wireOp",EDGE,"E151")}),1.0]])]});
            var Q4;
            {var subQ0=sQuery(id+"F1.wireOp",EDGE,"E129");Q4=makeQuery(id+"F1.imprint","IMPRINT",FACE,{"disambiguationData":[TD([[makeQuery(id+"F1.imprint","IMPRINT",EDGE,{"derivedFrom":subQ0}),-1.0]])]});}
            var Q5;
            Q5=makeQuery(id+"F1.imprint","IMPRINT",FACE,{"disambiguationData":[TD([[makeQuery(id+"F1.imprint","IMPRINT",EDGE,{"derivedFrom":sQuery(id+"F1.wireOp",EDGE,"E46")}),1.0]])]});
            var Q6;
            {var subQ0=sQuery(id+"F1.wireOp",EDGE,"E54");var subQ1=makeQuery(id+"F1.imprint","IMPRINT",VERTEX,{"disambiguationData":[OD(1.0)],"derivedFrom":subQ0});Q6=makeQuery(id+"F1.imprint","IMPRINT",FACE,{"disambiguationData":[TD([[makeQuery(id+"F1.imprint","IMPRINT",EDGE,{"disambiguationData":[TD([[subQ1,-1.0]])],"derivedFrom":subQ0}),1.0]])]});}
            var Q7;
            Q7=makeQuery(id+"F1.imprint","IMPRINT",FACE,{"disambiguationData":[TD([[makeQuery(id+"F1.imprint","IMPRINT",EDGE,{"derivedFrom":sQuery(id+"F1.wireOp",EDGE,"E69")}),1.0]])]});
            var Q8;
            Q8=makeQuery(id+"F1.imprint","IMPRINT",FACE,{"disambiguationData":[TD([[makeQuery(id+"F1.imprint","IMPRINT",EDGE,{"derivedFrom":sQuery(id+"F1.wireOp",EDGE,"E122")}),1.0]])]});
            var Q9;
            Q9=makeQuery(id+"F1.imprint","IMPRINT",FACE,{"disambiguationData":[TD([[makeQuery(id+"F1.imprint","IMPRINT",EDGE,{"derivedFrom":sQuery(id+"F1.wireOp",EDGE,"E138")}),1.0]])]});
            var Q10;
            Q10=makeQuery(id+"F1.imprint","IMPRINT",FACE,{"disambiguationData":[TD([[makeQuery(id+"F1.imprint","IMPRINT",EDGE,{"derivedFrom":sQuery(id+"F1.wireOp",EDGE,"E154")}),1.0]])]});
            var Q11;
            Q11=makeQuery(id+"F1.imprint","IMPRINT",FACE,{"disambiguationData":[TD([[makeQuery(id+"F1.imprint","IMPRINT",EDGE,{"derivedFrom":sQuery(id+"F1.wireOp",EDGE,"E136")}),1.0]])]});
            var Q12;
            {var subQ0=sQuery(id+"F0.wireOp",EDGE,"E17");var subQ1=sQuery(id+"F0.wireOp",EDGE,"E8");var subQ2=makeQuery(id+"F0.imprint","INTERSECT",VERTEX,{"derivedFrom":[subQ1,subQ0]});Q12=makeQuery(id+"F0.imprint","IMPRINT",FACE,{"disambiguationData":[TD([[makeQuery(id+"F0.imprint","IMPRINT",EDGE,{"disambiguationData":[TD([[subQ2,-1.0]])],"derivedFrom":subQ1}),1.0]])]});}
            var Q13;
            Q13=makeQuery(id+"F1.imprint","IMPRINT",FACE,{"disambiguationData":[TD([[makeQuery(id+"F1.imprint","IMPRINT",EDGE,{"derivedFrom":sQuery(id+"F1.wireOp",EDGE,"E137")}),1.0]])]});
            var Q14;
            {var subQ0=sQuery(id+"F1.wireOp",EDGE,"E133");Q14=makeQuery(id+"F1.imprint","IMPRINT",FACE,{"disambiguationData":[TD([[makeQuery(id+"F1.imprint","IMPRINT",EDGE,{"derivedFrom":subQ0}),-1.0]])]});}
            var Q15;
            {var subQ0=sQuery(id+"F1.wireOp",EDGE,"E131");Q15=makeQuery(id+"F1.imprint","IMPRINT",FACE,{"disambiguationData":[TD([[makeQuery(id+"F1.imprint","IMPRINT",EDGE,{"derivedFrom":subQ0}),-1.0]])]});}
            var Q16;
            Q16=makeQuery(id+"F1.imprint","IMPRINT",FACE,{"disambiguationData":[TD([[makeQuery(id+"F1.imprint","IMPRINT",EDGE,{"derivedFrom":sQuery(id+"F1.wireOp",EDGE,"E59")}),1.0]])]});
            var Q17;
            Q17=makeQuery(id+"F1.imprint","IMPRINT",FACE,{"disambiguationData":[TD([[makeQuery(id+"F1.imprint","IMPRINT",EDGE,{"derivedFrom":sQuery(id+"F1.wireOp",EDGE,"E87")}),1.0]])]});
            var Q18;
            {var subQ0=sQuery(id+"F1.wireOp",EDGE,"E89");var subQ1=sQuery(id+"F1.wireOp",EDGE,"E88");var subQ2=makeQuery(id+"F1.imprint","INTERSECT",VERTEX,{"derivedFrom":[subQ1,subQ0]});Q18=makeQuery(id+"F1.imprint","IMPRINT",FACE,{"disambiguationData":[TD([[makeQuery(id+"F1.imprint","IMPRINT",EDGE,{"disambiguationData":[TD([[subQ2,1.0]])],"derivedFrom":subQ1}),1.0]])]});}
            var Q19;
            {var subQ0=sQuery(id+"F1.wireOp",EDGE,"E72");var subQ1=sQuery(id+"F1.wireOp",EDGE,"E66");var subQ2=makeQuery(id+"F1.imprint","INTERSECT",VERTEX,{"derivedFrom":[subQ1,subQ0]});Q19=makeQuery(id+"F1.imprint","IMPRINT",FACE,{"disambiguationData":[TD([[makeQuery(id+"F1.imprint","IMPRINT",EDGE,{"disambiguationData":[TD([[subQ2,1.0]])],"derivedFrom":subQ1}),1.0]])]});}
            var Q20;
            {var subQ0=sQuery(id+"F1.wireOp",EDGE,"E134");var subQ1=sQuery(id+"F1.wireOp",EDGE,"E127");var subQ2=makeQuery(id+"F1.imprint","INTERSECT",VERTEX,{"disambiguationData":[OD(0.0)],"derivedFrom":[subQ1,subQ0]});Q20=makeQuery(id+"F1.imprint","IMPRINT",FACE,{"disambiguationData":[TD([[makeQuery(id+"F1.imprint","IMPRINT",EDGE,{"disambiguationData":[TD([[subQ2,1.0]])],"derivedFrom":subQ1}),-1.0]])]});}
            var Q21;
            Q21=makeQuery(id+"F1.imprint","IMPRINT",FACE,{"disambiguationData":[TD([[makeQuery(id+"F1.imprint","IMPRINT",EDGE,{"derivedFrom":sQuery(id+"F1.wireOp",EDGE,"E121")}),1.0]])]});
            var Q22;
            {var subQ0=sQuery(id+"F1.wireOp",EDGE,"E66");var subQ1=makeQuery(id+"F1.imprint","IMPRINT",VERTEX,{"derivedFrom":subQ0});Q22=makeQuery(id+"F1.imprint","IMPRINT",FACE,{"disambiguationData":[TD([[makeQuery(id+"F1.imprint","IMPRINT",EDGE,{"disambiguationData":[TD([[subQ1,1.0]])],"derivedFrom":subQ0}),1.0]])]});}
            var Q23;
            Q23=makeQuery(id+"F1.imprint","IMPRINT",FACE,{"disambiguationData":[TD([[makeQuery(id+"F1.imprint","IMPRINT",EDGE,{"derivedFrom":sQuery(id+"F1.wireOp",EDGE,"E139")}),1.0]])]});
            var Q24;
            Q24=makeQuery(id+"F1.imprint","IMPRINT",FACE,{"disambiguationData":[TD([[makeQuery(id+"F1.imprint","IMPRINT",EDGE,{"derivedFrom":sQuery(id+"F1.wireOp",EDGE,"E135")}),1.0]])]});
            var Q25;
            {var subQ0=sQuery(id+"F1.wireOp",EDGE,"E134");var subQ1=sQuery(id+"F1.wireOp",EDGE,"E127");var subQ2=makeQuery(id+"F1.imprint","INTERSECT",VERTEX,{"disambiguationData":[OD(0.0)],"derivedFrom":[subQ1,subQ0]});Q25=makeQuery(id+"F1.imprint","IMPRINT",FACE,{"disambiguationData":[TD([[makeQuery(id+"F1.imprint","IMPRINT",EDGE,{"disambiguationData":[TD([[subQ2,1.0]])],"derivedFrom":subQ1}),1.0]])]});}
            var Q26;
            Q26=makeQuery(id+"F1.imprint","IMPRINT",FACE,{"disambiguationData":[TD([[makeQuery(id+"F1.imprint","IMPRINT",EDGE,{"derivedFrom":sQuery(id+"F1.wireOp",EDGE,"E120")}),1.0]])]});
            var Q27;
            {var subQ0=sQuery(id+"F1.wireOp",EDGE,"E101");var subQ1=sQuery(id+"F1.wireOp",EDGE,"E78");var subQ2=makeQuery(id+"F1.imprint","INTERSECT",VERTEX,{"derivedFrom":[subQ1,subQ0]});Q27=makeQuery(id+"F1.imprint","IMPRINT",FACE,{"disambiguationData":[TD([[makeQuery(id+"F1.imprint","IMPRINT",EDGE,{"disambiguationData":[TD([[subQ2,-1.0]])],"derivedFrom":subQ1}),1.0]])]});}
            var Q28;
            {var subQ0=sQuery(id+"F1.wireOp",EDGE,"E80");var subQ1=sQuery(id+"F1.wireOp",EDGE,"E78");var subQ2=makeQuery(id+"F1.imprint","INTERSECT",VERTEX,{"derivedFrom":[subQ1,subQ0]});Q28=makeQuery(id+"F1.imprint","IMPRINT",FACE,{"disambiguationData":[TD([[makeQuery(id+"F1.imprint","IMPRINT",EDGE,{"disambiguationData":[TD([[subQ2,-1.0]])],"derivedFrom":subQ1}),-1.0]])]});}
            var Q29;
            Q29=makeQuery(id+"F1.imprint","IMPRINT",FACE,{"disambiguationData":[TD([[makeQuery(id+"F1.imprint","IMPRINT",EDGE,{"derivedFrom":sQuery(id+"F1.wireOp",EDGE,"E106")}),1.0]])]});
            var Q30;
            {var subQ0=sQuery(id+"F1.wireOp",EDGE,"E108");var subQ1=sQuery(id+"F1.wireOp",EDGE,"E107");var subQ2=makeQuery(id+"F1.imprint","INTERSECT",VERTEX,{"derivedFrom":[subQ1,subQ0]});Q30=makeQuery(id+"F1.imprint","IMPRINT",FACE,{"disambiguationData":[TD([[makeQuery(id+"F1.imprint","IMPRINT",EDGE,{"disambiguationData":[TD([[subQ2,1.0]])],"derivedFrom":subQ1}),1.0]])]});}
            var Q31;
            {var subQ0=sQuery(id+"F1.wireOp",EDGE,"E101");var subQ1=sQuery(id+"F1.wireOp",EDGE,"E78");var subQ2=makeQuery(id+"F1.imprint","INTERSECT",VERTEX,{"derivedFrom":[subQ1,subQ0]});Q31=makeQuery(id+"F1.imprint","IMPRINT",FACE,{"disambiguationData":[TD([[makeQuery(id+"F1.imprint","IMPRINT",EDGE,{"disambiguationData":[TD([[subQ2,-1.0]])],"derivedFrom":subQ1}),-1.0]])]});}
            var Q32;
            {var subQ1=sQuery(id+"F1.wireOp",EDGE,"E124.bottom");Q32=makeQuery(id+"F1.imprint","IMPRINT",FACE,{"disambiguationData":[TD([[makeQuery(id+"F1.imprint","IMPRINT",EDGE,{"derivedFrom":subQ1}),-1.0]])]});}
            var Q33;
            Q33=makeQuery(id+"F1.imprint","IMPRINT",FACE,{"disambiguationData":[TD([[makeQuery(id+"F1.imprint","IMPRINT",EDGE,{"derivedFrom":sQuery(id+"F1.wireOp",EDGE,"E159")}),1.0]])]});
            var Q34;
            Q34=makeQuery(id+"F1.imprint","IMPRINT",FACE,{"disambiguationData":[TD([[makeQuery(id+"F1.imprint","IMPRINT",EDGE,{"derivedFrom":sQuery(id+"F1.wireOp",EDGE,"E160")}),1.0]])]});
            var Q35;
            Q35=makeQuery(id+"F1.imprint","IMPRINT",FACE,{"disambiguationData":[TD([[makeQuery(id+"F1.imprint","IMPRINT",EDGE,{"derivedFrom":sQuery(id+"F1.wireOp",EDGE,"E156")}),1.0]])]});
            var Q36;
            Q36=makeQuery(id+"F1.imprint","IMPRINT",FACE,{"disambiguationData":[TD([[makeQuery(id+"F1.imprint","IMPRINT",EDGE,{"derivedFrom":sQuery(id+"F1.wireOp",EDGE,"E158")}),1.0]])]});
            var Q37;
            Q37=makeQuery(id+"F1.imprint","IMPRINT",FACE,{"disambiguationData":[TD([[makeQuery(id+"F1.imprint","IMPRINT",EDGE,{"derivedFrom":sQuery(id+"F1.wireOp",EDGE,"E155")}),1.0]])]});
            var Q38;
            Q38=makeQuery(id+"F1.imprint","IMPRINT",FACE,{"disambiguationData":[TD([[makeQuery(id+"F1.imprint","IMPRINT",EDGE,{"derivedFrom":sQuery(id+"F1.wireOp",EDGE,"E157")}),1.0]])]});
            extrude(context, id + "F2", {"entities" : qUnion([Q0, Q1, Q2, Q3, Q4, Q5, Q6, Q7, Q8, Q9, Q10, Q11, Q12, Q13, Q14, Q15, Q16, Q17, Q18, Q19, Q20, Q21, Q22, Q23, Q24, Q25, Q26, Q27, Q28, Q29, Q30, Q31, Q32, Q33, Q34, Q35, Q36, Q37, Q38]), "oppositeDirection" : true, "depth" : 1000 * mm, "offsetDistance" : 25 * mm});
        }
        {
            var Q0;
            {var subQ0=sQuery(id+"F0.wireOp",EDGE,"E23");Q0=makeQuery(id+"F0.imprint","IMPRINT",FACE,{"disambiguationData":[TD([[makeQuery(id+"F0.imprint","IMPRINT",EDGE,{"derivedFrom":subQ0}),1.0]])]});}
            var Q1;
            {var subQ0=sQuery(id+"F0.wireOp",EDGE,"E26");Q1=makeQuery(id+"F0.imprint","IMPRINT",FACE,{"disambiguationData":[TD([[makeQuery(id+"F0.imprint","IMPRINT",EDGE,{"derivedFrom":subQ0}),1.0]])]});}
            var Q2;
            {var subQ0=sQuery(id+"F0.wireOp",EDGE,"E22");Q2=makeQuery(id+"F0.imprint","IMPRINT",FACE,{"disambiguationData":[TD([[makeQuery(id+"F0.imprint","IMPRINT",EDGE,{"derivedFrom":subQ0}),-1.0]])]});}
            var Q3;
            {var subQ0=sQuery(id+"F0.wireOp",EDGE,"E13");Q3=makeQuery(id+"F0.imprint","IMPRINT",FACE,{"disambiguationData":[TD([[makeQuery(id+"F0.imprint","IMPRINT",EDGE,{"derivedFrom":subQ0}),1.0]])]});}
            var Q4;
            {var subQ0=sQuery(id+"F0.wireOp",EDGE,"E16");Q4=makeQuery(id+"F0.imprint","IMPRINT",FACE,{"disambiguationData":[TD([[makeQuery(id+"F0.imprint","IMPRINT",EDGE,{"derivedFrom":subQ0}),1.0]])]});}
            var Q5;
            {var subQ0=sQuery(id+"F0.wireOp",EDGE,"E20");Q5=makeQuery(id+"F0.imprint","IMPRINT",FACE,{"disambiguationData":[TD([[makeQuery(id+"F0.imprint","IMPRINT",EDGE,{"derivedFrom":subQ0}),1.0]])]});}
            var Q6;
            {var subQ3=sQuery(id+"F0.wireOp",EDGE,"E37.bottom");Q6=makeQuery(id+"F0.imprint","IMPRINT",FACE,{"disambiguationData":[TD([[makeQuery(id+"F0.imprint","IMPRINT",EDGE,{"derivedFrom":subQ3}),1.0]])]});}
            extrude(context, id + "F3", {"entities" : qUnion([Q0, Q1, Q2, Q3, Q4, Q5, Q6]), "depth" : 2500 * mm, "offsetDistance" : 25 * mm});
        }
        {
            var Q0;
            Q0 = qSketchRegion(id + "F1", true);
            extrude(context, id + "F4", {"entities" : qUnion([Q0]), "depth" : 25 * mm, "offsetDistance" : 25 * mm});
        }
        {
            var Q0;
            Q0 = qSketchRegion(id + "F1", true);
            var Q1;
            Q1 = qSketchRegion(id + "F0", true);
            extrude(context, id + "F5", {"entities" : qUnion([Q0, Q1]), "depth" : 25 * mm, "offsetDistance" : 25 * mm});
        }
        {
            var Q0;
            Q0 = qSketchRegion(id + "F1", true);
            extrude(context, id + "F6", {"entities" : qUnion([Q0]), "depth" : 25 * mm, "offsetDistance" : 25 * mm});
        }
        {
            var Q0;
            Q0 = qSketchRegion(id + "F1", true);
            extrude(context, id + "F7", {"entities" : qUnion([Q0]), "depth" : 25 * mm, "offsetDistance" : 25 * mm});
        }
        {
            var Q0;
            Q0 = qSketchRegion(id + "F1", true);
            extrude(context, id + "F8", {"entities" : qUnion([Q0]), "depth" : 25 * mm, "offsetDistance" : 25 * mm});
        }
    });
